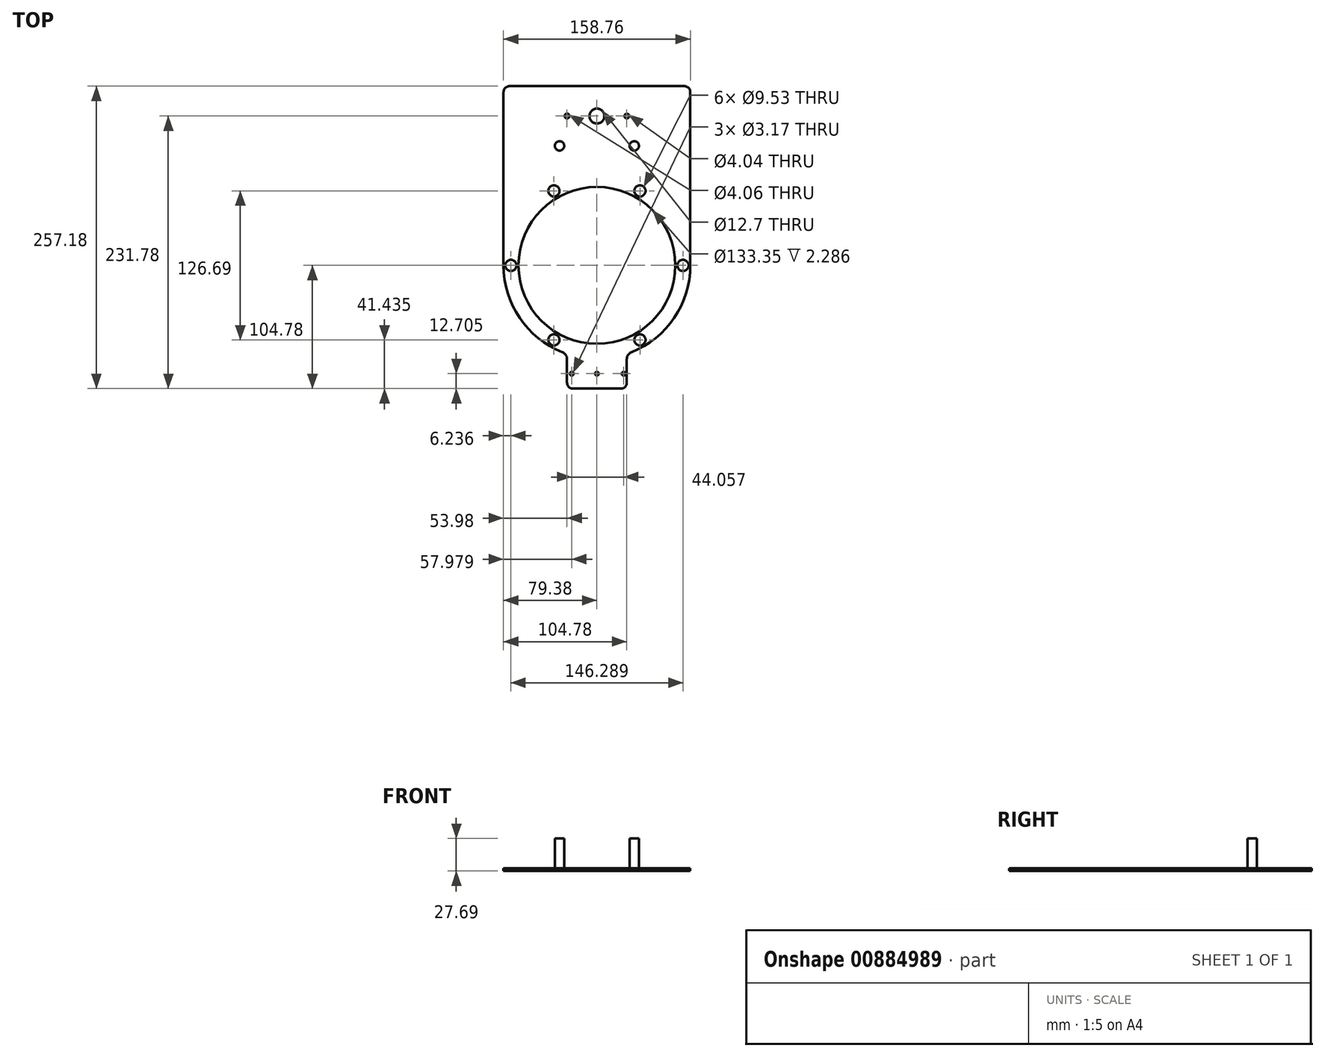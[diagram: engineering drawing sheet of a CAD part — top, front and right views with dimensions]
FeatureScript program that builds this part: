
annotation { "Feature Type Name" : "Feature", "Feature Type Description" : "" }
export const myFeature = defineFeature(function(context is Context, id is Id, definition is map)
    precondition{}
    {
        {
            var Q0;
            Q0=qCreatedBy(makeId("Top.planeOp"),FACE);
            var sketch = newSketch(context, id + "F0", { "sketchPlane" : qUnion([Q0])});
            skCircle(sketch, "E0", {"center": v(0, 0) * mm, "radius": 66.68 * mm});
            skArc(sketch, "E1", {"start": v(-79.38, 0) * mm, "mid": v(-65.7, -44.54) * mm, "end": v(-29.4, -73.73) * mm});
            skLineSegment(sketch, "E2", {"start": v(-79.38, 0) * mm, "end": v(-79.38, 152.4) * mm});
            skLineSegment(sketch, "E3", {"start": v(79.38, 0) * mm, "end": v(79.38, 152.4) * mm});
            skLineSegment(sketch, "E4", {"start": v(79.38, 152.4) * mm, "end": v(-79.38, 152.4) * mm});
            skCircle(sketch, "E5", {"center": v(0, 127) * mm, "radius": 6.35 * mm});
            skCircle(sketch, "E6", {"center": v(-73.14, 0) * mm, "radius": 4.76 * mm});
            skCircle(sketch, "E7.1.1", {"center": v(-36.57, -63.34) * mm, "radius": 4.76 * mm});
            skCircle(sketch, "E7.2.1", {"center": v(36.57, -63.34) * mm, "radius": 4.76 * mm});
            skCircle(sketch, "E7.3.1", {"center": v(73.14, 0) * mm, "radius": 4.76 * mm});
            skCircle(sketch, "E7.4.1", {"center": v(36.57, 63.34) * mm, "radius": 4.76 * mm});
            skCircle(sketch, "E7.5.1", {"center": v(-36.57, 63.34) * mm, "radius": 4.76 * mm});
            skCircle(sketch, "E8", {"center": v(0, 0) * mm, "radius": 79.38 * mm});
            skCircle(sketch, "E9", {"center": v(25.4, 127) * mm, "radius": 2.02 * mm});
            skCircle(sketch, "E10", {"center": v(-25.4, 127) * mm, "radius": 2.03 * mm});
            skLineSegment(sketch, "E11.top", {"start": v(0, -104.78) * mm, "end": v(-25.4, -104.78) * mm});
            skLineSegment(sketch, "E11.right", {"start": v(-25.4, -79.63) * mm, "end": v(-25.4, -104.78) * mm});
            skLineSegment(sketch, "E12.top", {"start": v(0, -104.78) * mm, "end": v(25.4, -104.78) * mm});
            skLineSegment(sketch, "E12.right", {"start": v(25.4, -79.38) * mm, "end": v(25.4, -104.78) * mm});
            skPoint(sketch, "E13.newPointB", {"position": v(-25.4, -79.38) * mm});
            skArc(sketch, "E13.filletArc", {"start": v(-25.4, -79.63) * mm, "mid": v(-26.5, -76.07) * mm, "end": v(-29.4, -73.73) * mm});
            skArc(sketch, "E14.MirrorCS", {"start": v(25.4, -79.63) * mm, "mid": v(26.5, -76.07) * mm, "end": v(29.4, -73.73) * mm});
            skCircle(sketch, "E15", {"center": v(-21.4, -92.08) * mm, "radius": 1.59 * mm});
            skCircle(sketch, "E16", {"center": v(0, -92.08) * mm, "radius": 1.59 * mm});
            skCircle(sketch, "E17", {"center": v(22.66, -92.08) * mm, "radius": 1.59 * mm});
            skSolve(sketch);
        }
        {
            var Q0;
            Q0 = qSketchRegion(id + "F0", true);
            extrude(context, id + "F1", {"entities" : qUnion([Q0]), "depth" : 2.3 * mm, "offsetDistance" : 25.4 * mm});
        }
        {
            var Q0;
            Q0=makeQuery(id+"F1.opExtrude","SWEPT_EDGE",EDGE,{"disambiguationData":[OSD([sQuery(id+"F0.wireOp",EDGE,"E2"),sQuery(id+"F0.wireOp",EDGE,"E4")])]});
            var Q1;
            Q1=makeQuery(id+"F1.opExtrude","SWEPT_EDGE",EDGE,{"disambiguationData":[OSD([sQuery(id+"F0.wireOp",EDGE,"E3"),sQuery(id+"F0.wireOp",EDGE,"E4")])]});
            fillet(context, id + "F2", {"entities" : qUnion([Q0, Q1]), "radius" : 5.08 * mm, "tangentPropagation" : true, "allowEdgeOverflow" : false});
        }
        {
            var Q0;
            Q0=makeQuery(id+"F1.opExtrude","SWEPT_EDGE",EDGE,{"disambiguationData":[OSD([sQuery(id+"F0.wireOp",EDGE,"E12.top"),sQuery(id+"F0.wireOp",EDGE,"E12.right")])]});
            var Q1;
            Q1=makeQuery(id+"F1.opExtrude","SWEPT_EDGE",EDGE,{"disambiguationData":[OSD([sQuery(id+"F0.wireOp",EDGE,"E11.top"),sQuery(id+"F0.wireOp",EDGE,"E11.right")])]});
            fillet(context, id + "F3", {"entities" : qUnion([Q0, Q1]), "radius" : 5.08 * mm, "tangentPropagation" : true, "allowEdgeOverflow" : false});
        }
        {
            var Q0;
            Q0=makeQuery(id+"F1.opExtrude","CAP_FACE",FACE,{"disambiguationData":[OSD([sQuery(id+"F0.wireOp",EDGE,"E2"),sQuery(id+"F0.wireOp",EDGE,"E3"),sQuery(id+"F0.wireOp",EDGE,"E4"),sQuery(id+"F0.wireOp",EDGE,"E5"),sQuery(id+"F0.wireOp",EDGE,"E6"),sQuery(id+"F0.wireOp",EDGE,"E7.1.1"),sQuery(id+"F0.wireOp",EDGE,"E7.2.1"),sQuery(id+"F0.wireOp",EDGE,"E7.3.1"),sQuery(id+"F0.wireOp",EDGE,"E7.4.1"),sQuery(id+"F0.wireOp",EDGE,"E0"),sQuery(id+"F0.wireOp",EDGE,"E7.5.1"),sQuery(id+"F0.wireOp",EDGE,"E8"),sQuery(id+"F0.wireOp",EDGE,"E9"),sQuery(id+"F0.wireOp",EDGE,"E10"),sQuery(id+"F0.wireOp",EDGE,"E11.top"),sQuery(id+"F0.wireOp",EDGE,"E11.right"),sQuery(id+"F0.wireOp",EDGE,"E12.top"),sQuery(id+"F0.wireOp",EDGE,"E12.right"),sQuery(id+"F0.wireOp",EDGE,"E13.filletArc"),sQuery(id+"F0.wireOp",EDGE,"E14.MirrorCS"),sQuery(id+"F0.wireOp",EDGE,"E15"),sQuery(id+"F0.wireOp",EDGE,"E16"),sQuery(id+"F0.wireOp",EDGE,"E17")])],"isStart":false});
            var sketch = newSketch(context, id + "F4", { "sketchPlane" : qUnion([Q0])});
            skCircle(sketch, "E18", {"center": v(-31.75, 101.6) * mm, "radius": 4 * mm});
            skCircle(sketch, "E19", {"center": v(31.75, 101.6) * mm, "radius": 4 * mm});
            skSolve(sketch);
        }
        {
            var Q0;
            Q0 = qSketchRegion(id + "F4", true);
            extrude(context, id + "F5", {"entities" : qUnion([Q0]), "operationType" : NewBodyOperationType.ADD, "depth" : 25.4 * mm, "offsetDistance" : 25.4 * mm});
        }
    });
